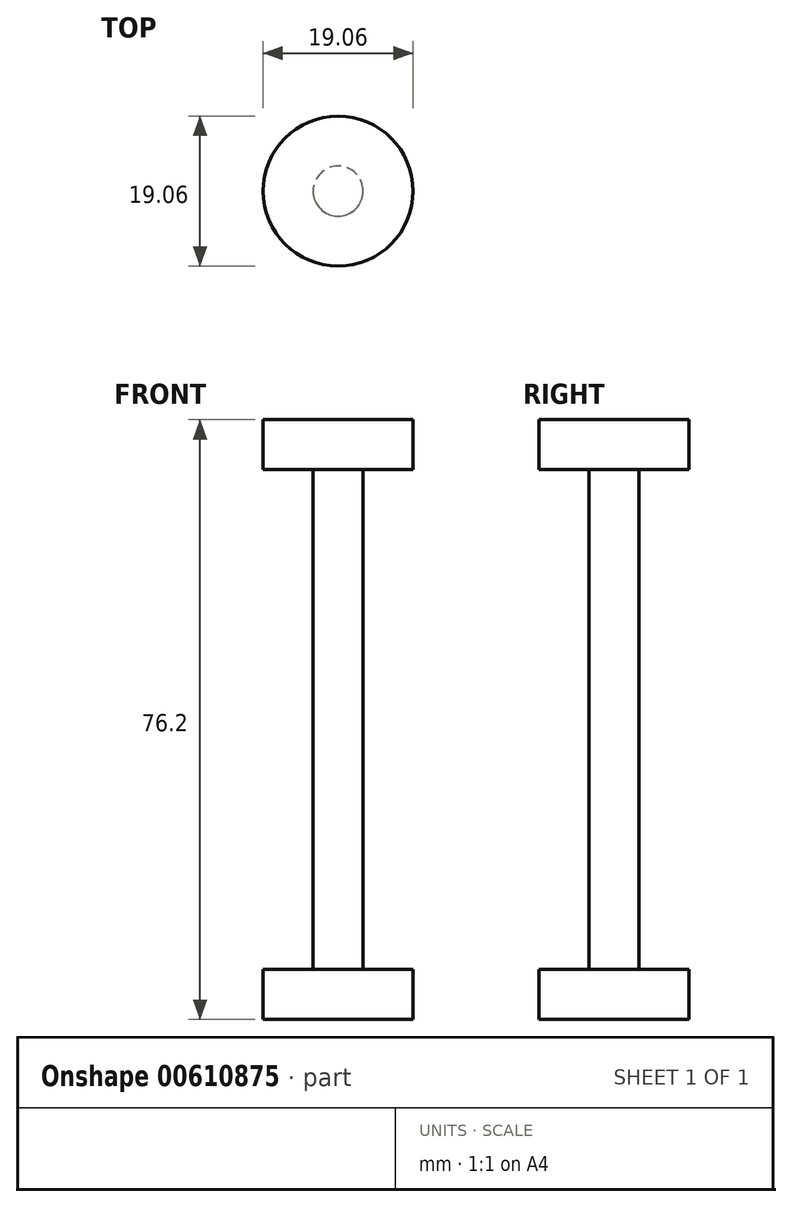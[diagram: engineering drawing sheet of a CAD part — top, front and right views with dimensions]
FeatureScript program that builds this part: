
annotation { "Feature Type Name" : "Feature", "Feature Type Description" : "" }
export const myFeature = defineFeature(function(context is Context, id is Id, definition is map)
    precondition{}
    {
        {
            var Q0;
            Q0=qCreatedBy(makeId("Top.planeOp"),FACE);
            var sketch = newSketch(context, id + "F0", { "sketchPlane" : qUnion([Q0])});
            skCircle(sketch, "E0", {"center": v(0, 0) * mm, "radius": 3.17 * mm});
            skSolve(sketch);
        }
        {
            var Q0;
            Q0 = qSketchRegion(id + "F0", true);
            extrude(context, id + "F1", {"entities" : qUnion([Q0]), "endBound" : BoundingType.SYMMETRIC, "depth" : 76.2 * mm, "offsetDistance" : 25.4 * mm});
        }
        {
            var Q0;
            Q0=makeQuery(id+"F1.opExtrude","CAP_FACE",FACE,{"disambiguationData":[OSD([sQuery(id+"F0.wireOp",EDGE,"E0")])],"isStart":false});
            var sketch = newSketch(context, id + "F2", { "sketchPlane" : qUnion([Q0])});
            skCircle(sketch, "E1", {"center": v(0, 0) * mm, "radius": 9.53 * mm});
            skSolve(sketch);
        }
        {
            var Q0;
            Q0 = qSketchRegion(id + "F2", true);
            extrude(context, id + "F3", {"entities" : qUnion([Q0]), "operationType" : NewBodyOperationType.ADD, "oppositeDirection" : true, "depth" : 6.35 * mm, "offsetDistance" : 25.4 * mm});
        }
        {
            var Q0;
            Q0=makeQuery(id+"F1.opExtrude","CAP_FACE",FACE,{"disambiguationData":[OSD([sQuery(id+"F0.wireOp",EDGE,"E0")])],"isStart":true});
            var sketch = newSketch(context, id + "F4", { "sketchPlane" : qUnion([Q0])});
            skCircle(sketch, "E2", {"center": v(0, 0) * mm, "radius": 9.53 * mm});
            skSolve(sketch);
        }
        {
            var Q0;
            Q0 = qSketchRegion(id + "F4", true);
            extrude(context, id + "F5", {"entities" : qUnion([Q0]), "operationType" : NewBodyOperationType.ADD, "oppositeDirection" : true, "depth" : 6.35 * mm, "offsetDistance" : 25.4 * mm});
        }
        {
            var Q0;
            Q0=makeQuery(id+"F3.opExtrude","CAP_FACE",FACE,{"disambiguationData":[OSD([sQuery(id+"F2.wireOp",EDGE,"E1")])],"isStart":false});
            var sketch = newSketch(context, id + "F6", { "sketchPlane" : qUnion([Q0])});
            skCircle(sketch, "E3", {"center": v(0, 0) * mm, "radius": 3.3 * mm});
            skSolve(sketch);
        }
    });
